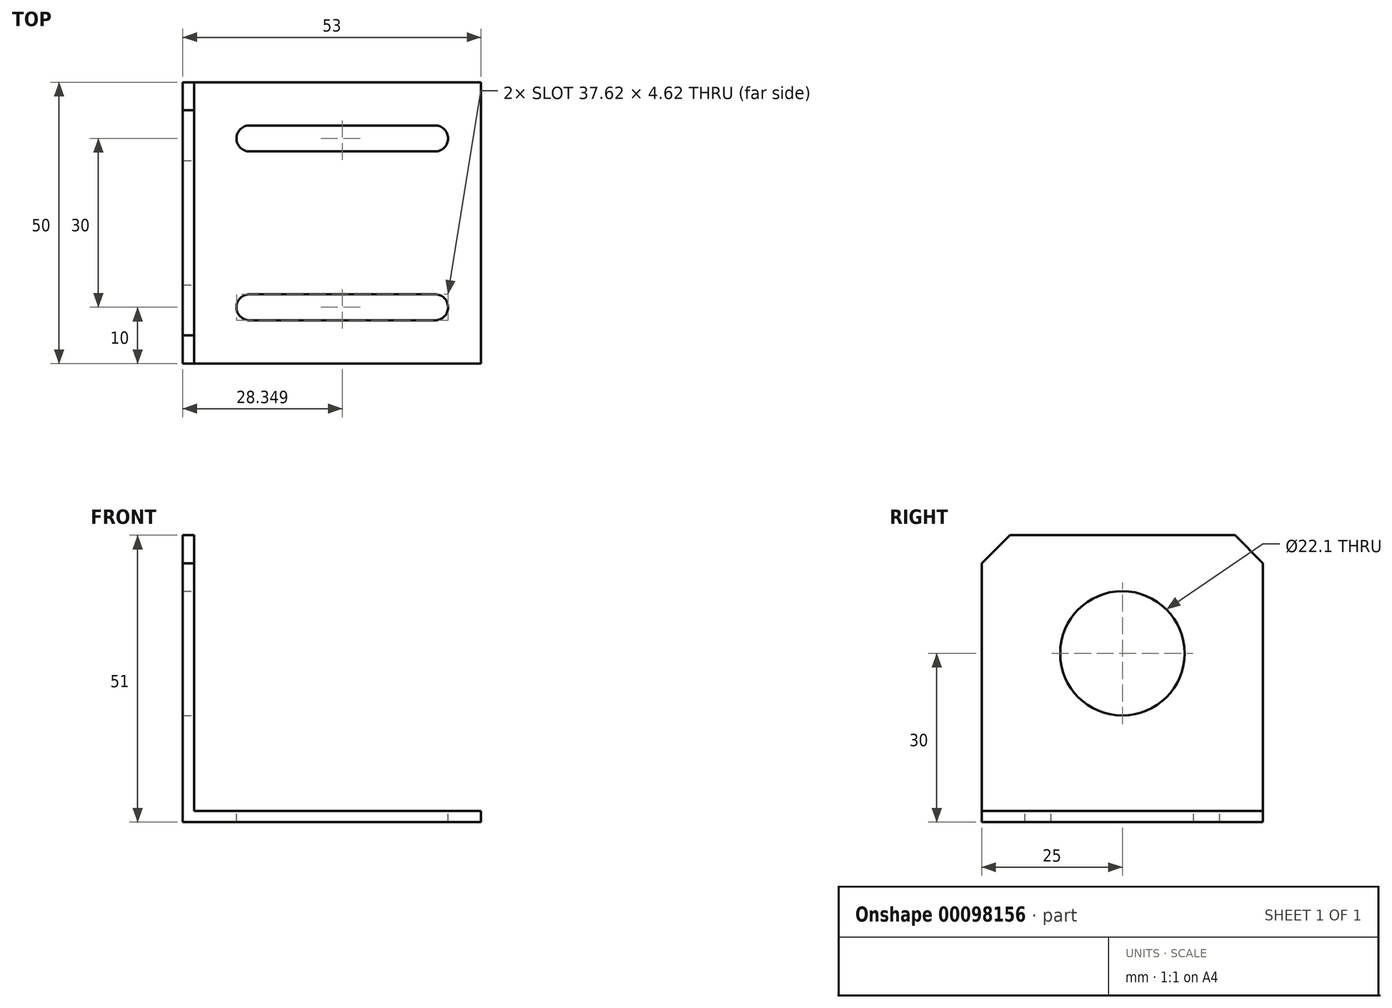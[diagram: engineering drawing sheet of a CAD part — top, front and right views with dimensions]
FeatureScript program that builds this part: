
annotation { "Feature Type Name" : "Feature", "Feature Type Description" : "" }
export const myFeature = defineFeature(function(context is Context, id is Id, definition is map)
    precondition{}
    {
        {
            var Q0;
            Q0=qCreatedBy(makeId("Front.planeOp"),FACE);
            var sketch = newSketch(context, id + "F0", { "sketchPlane" : qUnion([Q0])});
            skLineSegment(sketch, "E0", {"start": v(-58.33, 78.79) * mm, "end": v(-58.33, 27.79) * mm});
            skLineSegment(sketch, "E1", {"start": v(-58.33, 27.79) * mm, "end": v(-5.33, 27.79) * mm});
            skLineSegment(sketch, "E2", {"start": v(-5.33, 27.79) * mm, "end": v(-5.33, 29.79) * mm});
            skLineSegment(sketch, "E3", {"start": v(-5.33, 29.79) * mm, "end": v(-56.33, 29.79) * mm});
            skLineSegment(sketch, "E4", {"start": v(-56.33, 29.79) * mm, "end": v(-56.33, 78.79) * mm});
            skLineSegment(sketch, "E5", {"start": v(-56.33, 78.79) * mm, "end": v(-58.33, 78.79) * mm});
            skSolve(sketch);
        }
        {
            var Q0;
            Q0=makeQuery(id+"F0.imprint","IMPRINT",FACE,{"disambiguationData":[TD([[makeQuery(id+"F0.imprint","IMPRINT",EDGE,{"derivedFrom":sQuery(id+"F0.wireOp",EDGE,"E0")}),1.0]])]});
            extrude(context, id + "F1", {"entities" : qUnion([Q0]), "oppositeDirection" : true, "depth" : 50 * mm});
        }
        {
            var Q0;
            Q0=makeQuery(id+"F1.opExtrude","SWEPT_FACE",FACE,{"disambiguationData":[OSD([sQuery(id+"F0.wireOp",EDGE,"E4")])]});
            var sketch = newSketch(context, id + "F2", { "sketchPlane" : qUnion([Q0])});
            skCircle(sketch, "E6", {"center": v(25, 57.79) * mm, "radius": 11.05 * mm});
            skLineSegment(sketch, "E7", {"start": v(0, 73.79) * mm, "end": v(5, 78.79) * mm});
            skLineSegment(sketch, "E8", {"start": v(45, 78.79) * mm, "end": v(50, 73.79) * mm});
            skSolve(sketch);
        }
        {
            var Q0;
            Q0=makeQuery(id+"F2.imprint","IMPRINT",FACE,{"disambiguationData":[TD([[makeQuery(id+"F2.imprint","IMPRINT",EDGE,{"derivedFrom":sQuery(id+"F2.wireOp",EDGE,"E6")}),1.0]])]});
            var Q1;
            {var subQ0=sQuery(id+"F2.wireOp",EDGE,"E7");Q1=makeQuery(id+"F2.imprint","IMPRINT",FACE,{"disambiguationData":[TD([[makeQuery(id+"F2.imprint","IMPRINT",EDGE,{"derivedFrom":subQ0}),1.0]])]});}
            var Q2;
            {var subQ0=sQuery(id+"F2.wireOp",EDGE,"E8");Q2=makeQuery(id+"F2.imprint","IMPRINT",FACE,{"disambiguationData":[TD([[makeQuery(id+"F2.imprint","IMPRINT",EDGE,{"derivedFrom":subQ0}),1.0]])]});}
            extrude(context, id + "F3", {"entities" : qUnion([Q0, Q1, Q2]), "operationType" : NewBodyOperationType.REMOVE, "oppositeDirection" : true, "depth" : 2 * mm});
        }
        {
            var Q0;
            Q0=makeQuery(id+"F1.opExtrude","SWEPT_FACE",FACE,{"disambiguationData":[OSD([sQuery(id+"F0.wireOp",EDGE,"E3")])]});
            var sketch = newSketch(context, id + "F4", { "sketchPlane" : qUnion([Q0])});
            skLineSegment(sketch, "E9", {"start": v(-46.48, 7.69) * mm, "end": v(-13.48, 7.69) * mm});
            skLineSegment(sketch, "E10", {"start": v(-46.48, 12.31) * mm, "end": v(-13.48, 12.31) * mm});
            skArc(sketch, "E11", {"start": v(-46.48, 12.31) * mm, "mid": v(-48.8, 10) * mm, "end": v(-46.48, 7.69) * mm});
            skArc(sketch, "E12", {"start": v(-13.48, 7.69) * mm, "mid": v(-11.17, 10) * mm, "end": v(-13.48, 12.31) * mm});
            skLineSegment(sketch, "E13", {"start": v(-55.7, 25) * mm, "end": v(-8.95, 25) * mm, "construction": true});
            skLineSegment(sketch, "E14.MirrorCS", {"start": v(-46.48, 37.69) * mm, "end": v(-13.48, 37.69) * mm});
            skLineSegment(sketch, "E15.MirrorCS", {"start": v(-46.48, 42.31) * mm, "end": v(-13.48, 42.31) * mm});
            skArc(sketch, "E16.MirrorCS", {"start": v(-13.48, 42.31) * mm, "mid": v(-11.17, 40) * mm, "end": v(-13.48, 37.69) * mm});
            skArc(sketch, "E17.MirrorCS", {"start": v(-46.48, 37.69) * mm, "mid": v(-48.8, 40) * mm, "end": v(-46.48, 42.31) * mm});
            skSolve(sketch);
        }
        {
            var Q0;
            Q0=makeQuery(id+"F4.imprint","IMPRINT",FACE,{"disambiguationData":[TD([[makeQuery(id+"F4.imprint","IMPRINT",EDGE,{"derivedFrom":sQuery(id+"F4.wireOp",EDGE,"E9")}),1.0]])]});
            var Q1;
            Q1=makeQuery(id+"F4.imprint","IMPRINT",FACE,{"disambiguationData":[TD([[makeQuery(id+"F4.imprint","IMPRINT",EDGE,{"derivedFrom":sQuery(id+"F4.wireOp",EDGE,"E14.MirrorCS")}),1.0]])]});
            extrude(context, id + "F5", {"entities" : qUnion([Q0, Q1]), "operationType" : NewBodyOperationType.REMOVE, "oppositeDirection" : true, "depth" : 2 * mm});
        }
    });
